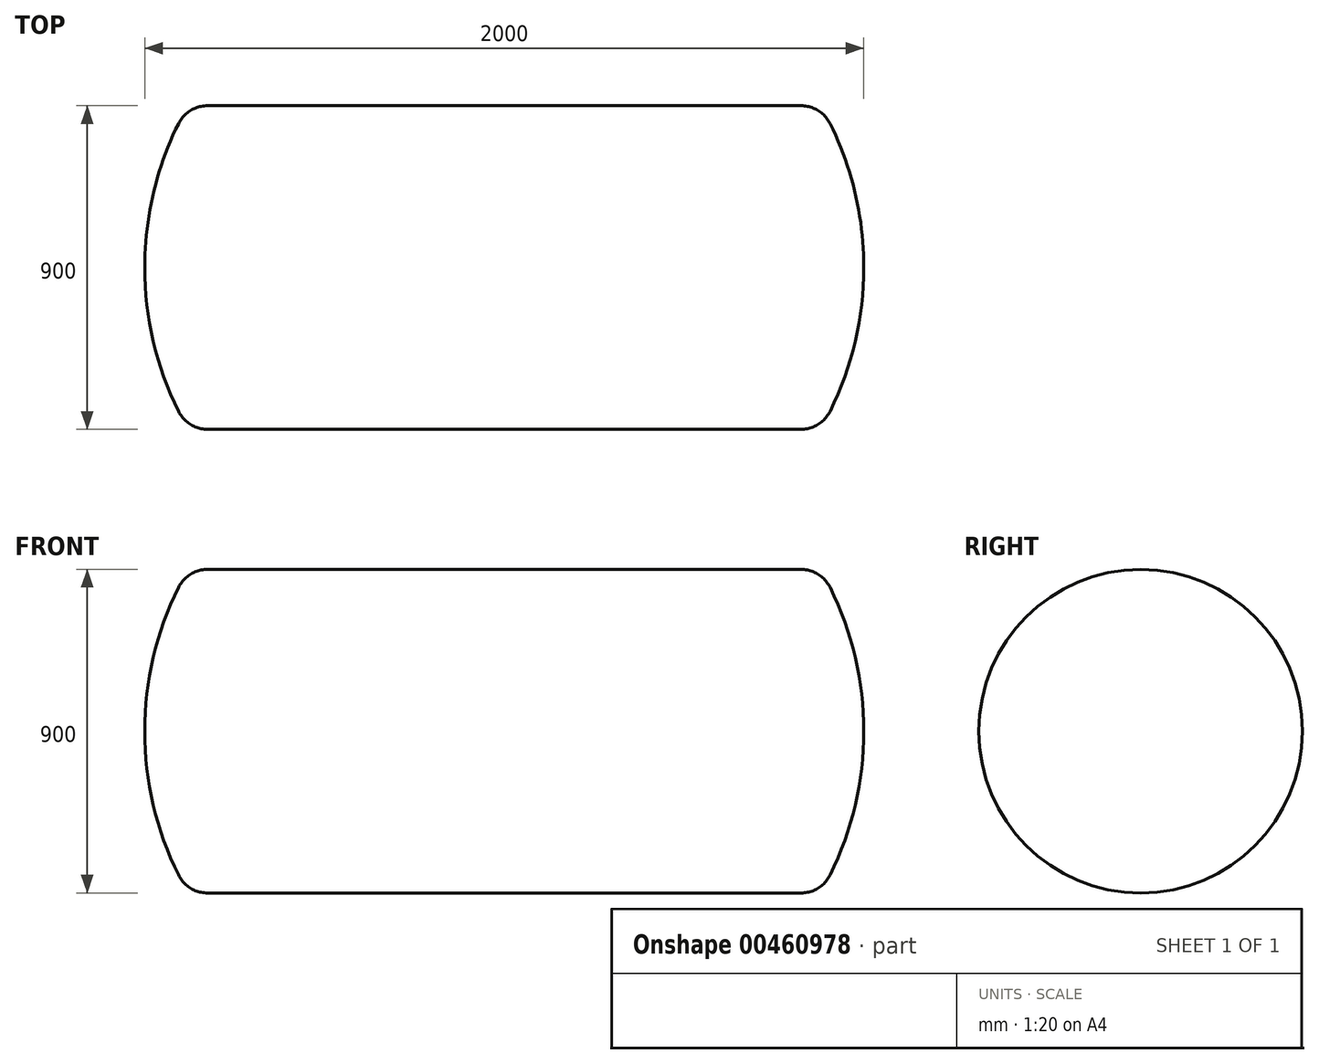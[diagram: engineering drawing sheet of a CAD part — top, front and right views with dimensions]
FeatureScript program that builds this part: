
annotation { "Feature Type Name" : "Feature", "Feature Type Description" : "" }
export const myFeature = defineFeature(function(context is Context, id is Id, definition is map)
    precondition{}
    {
        {
            var Q0;
            Q0=qCreatedBy(makeId("Top.planeOp"),FACE);
            var sketch = newSketch(context, id + "F0", { "sketchPlane" : qUnion([Q0])});
            skLineSegment(sketch, "E0", {"start": v(0, 450) * mm, "end": v(-825.6, 450) * mm});
            skLineSegment(sketch, "E1", {"start": v(958.15, 0) * mm, "end": v(-818.12, 0) * mm, "construction": true});
            skArc(sketch, "E2", {"start": v(-906.23, 400) * mm, "mid": v(-976.24, 205.42) * mm, "end": v(-1000, 0) * mm});
            skPoint(sketch, "E3.visualSharp", {"position": v(-879.42, 450) * mm});
            skArc(sketch, "E3.filletArc", {"start": v(-825.6, 450) * mm, "mid": v(-873.04, 436.49) * mm, "end": v(-906.23, 400) * mm});
            skLineSegment(sketch, "E4", {"start": v(0, 574) * mm, "end": v(0, -614.97) * mm, "construction": true});
            skLineSegment(sketch, "E5", {"start": v(-1000, 0) * mm, "end": v(0, 0) * mm});
            skLineSegment(sketch, "E6", {"start": v(0, 0) * mm, "end": v(0, 450) * mm});
            skSolve(sketch);
        }
        {
            var Q0;
            Q0 = qSketchRegion(id + "F0", true);
            var Q1;
            Q1=sQuery(id+"F0.wireOp",EDGE,"E1");
            revolve(context, id + "F1", {"entities" : qUnion([Q0]), "axis" : qUnion([Q1]), "revolveType" : RevolveType.FULL});
        }
        {
            var Q0;
            Q0=makeQuery(id+"F1.opRevolve","SWEPT_BODY",BODY,{"disambiguationData":[OSD([sQuery(id+"F0.wireOp",EDGE,"E0"),sQuery(id+"F0.wireOp",EDGE,"E2"),sQuery(id+"F0.wireOp",EDGE,"E3.filletArc"),sQuery(id+"F0.wireOp",EDGE,"E5"),sQuery(id+"F0.wireOp",EDGE,"E6")])]});
            var Q1;
            Q1=makeQuery(id+"F1.opRevolve","SWEPT_FACE",FACE,{"disambiguationData":[OSD([sQuery(id+"F0.wireOp",EDGE,"E6")])]});
            mirror(context, id + "F2", {"operationType" : NewBodyOperationType.ADD, "entities" : qUnion([Q0]), "mirrorPlane" : qUnion([Q1])});
        }
    });
